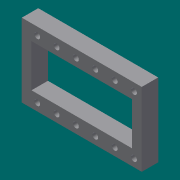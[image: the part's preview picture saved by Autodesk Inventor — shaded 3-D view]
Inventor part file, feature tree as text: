
AUTODESK INVENTOR PART (.ipt)
format: ipt  version: 2013 (Build 170138000, 138)  size: 98,304 bytes
history: native  units: mm
features: extrude x2, sketch x2, other x1
ambient origin geometry x8: Origin, YZ Plane, XZ Plane, XY Plane, X Axis, Y Axis, Z Axis, Center Point
feature tree (5):
  other  "ソリッド1"
  extrude  "押し出し1"  Depth=8.5mm TaperAngle=0.0deg
  extrude  "押し出し2"  Depth=5.0mm
  sketch  "スケッチ1"
  sketch  "スケッチ2"
